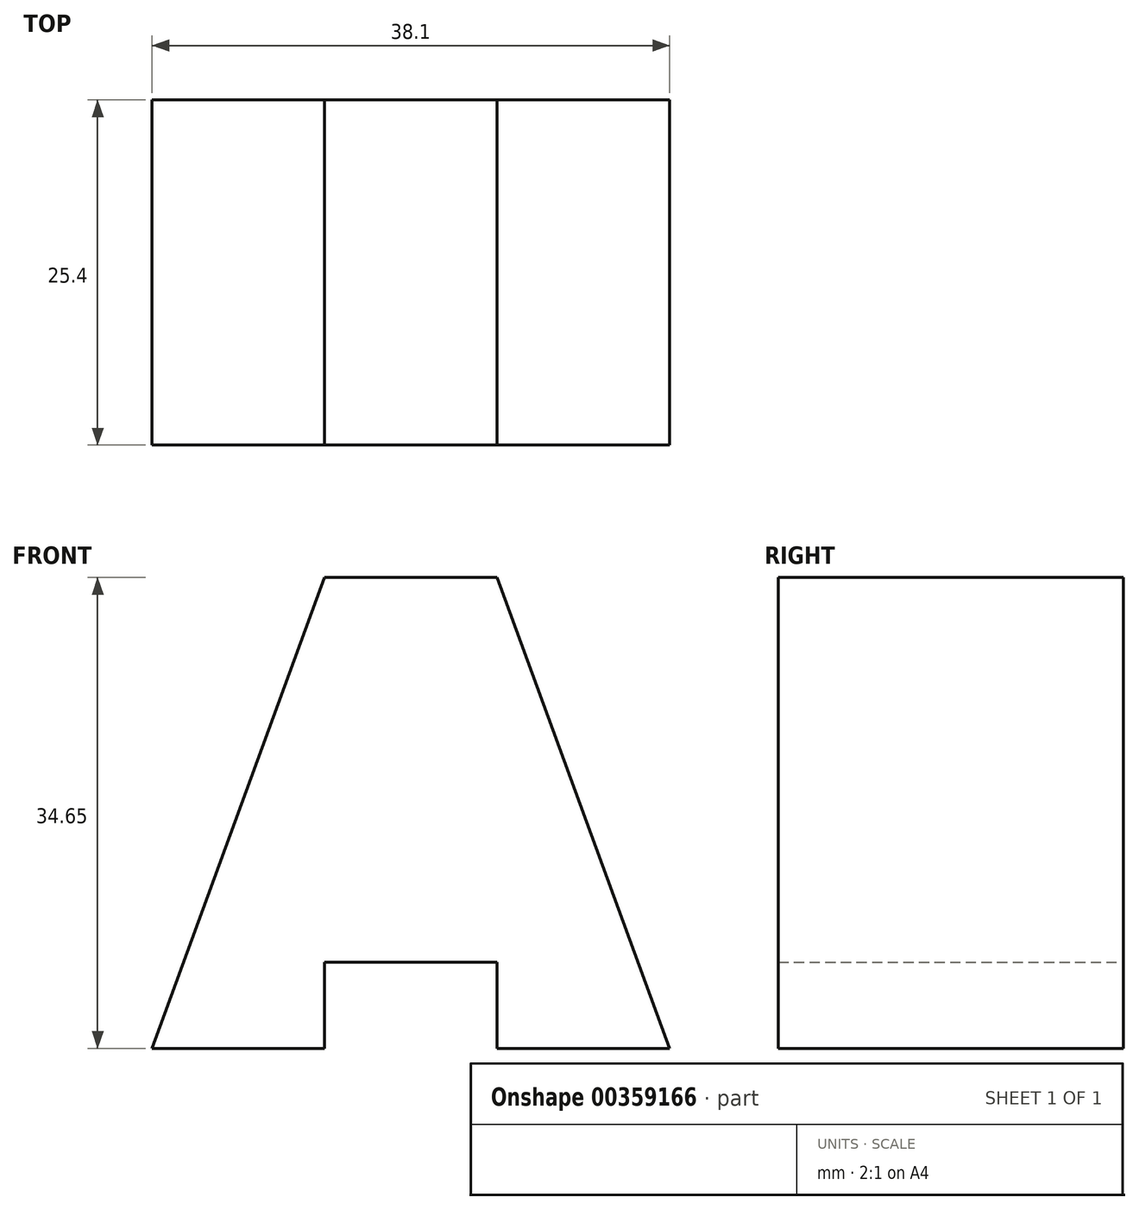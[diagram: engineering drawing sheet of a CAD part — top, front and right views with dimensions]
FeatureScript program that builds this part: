
annotation { "Feature Type Name" : "Feature", "Feature Type Description" : "" }
export const myFeature = defineFeature(function(context is Context, id is Id, definition is map)
    precondition{}
    {
        {
            var Q0;
            Q0=qCreatedBy(makeId("Front.planeOp"),FACE);
            var sketch = newSketch(context, id + "F0", { "sketchPlane" : qUnion([Q0])});
            skLineSegment(sketch, "E0", {"start": v(0, 0) * mm, "end": v(12.7, 34.65) * mm});
            skLineSegment(sketch, "E1", {"start": v(12.7, 34.65) * mm, "end": v(25.4, 34.65) * mm});
            skLineSegment(sketch, "E2", {"start": v(25.4, 34.65) * mm, "end": v(38.1, 0) * mm});
            skLineSegment(sketch, "E3", {"start": v(38.1, 0) * mm, "end": v(25.4, 0) * mm});
            skLineSegment(sketch, "E4", {"start": v(25.4, 0) * mm, "end": v(25.4, 6.35) * mm});
            skLineSegment(sketch, "E5", {"start": v(25.4, 6.35) * mm, "end": v(12.7, 6.35) * mm});
            skLineSegment(sketch, "E6", {"start": v(12.7, 6.35) * mm, "end": v(12.7, 0) * mm});
            skLineSegment(sketch, "E7", {"start": v(12.7, 0) * mm, "end": v(0, 0) * mm});
            skSolve(sketch);
        }
        {
            var Q0;
            Q0 = qSketchRegion(id + "F0", true);
            extrude(context, id + "F1", {"entities" : qUnion([Q0]), "depth" : 25.4 * mm});
        }
    });
